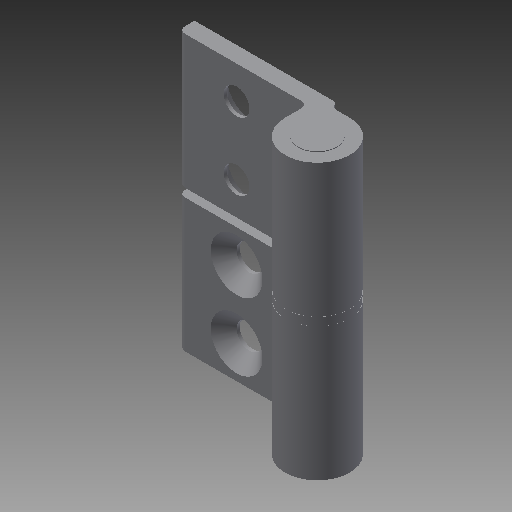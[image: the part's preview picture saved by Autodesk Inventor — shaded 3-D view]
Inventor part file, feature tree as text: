
AUTODESK INVENTOR PART (.ipt)
format: ipt  version: 2018 (Build 220112000, 112)  size: 186,880 bytes
history: native  units: mm
features: other x42, sketch x8, extrude x4, hole x4
ambient origin geometry x8: Origin, YZ Plane, XZ Plane, XY Plane, X Axis, Y Axis, Z Axis, Center Point
bodies: Solid1 (feature_tree)
feature tree (58):
  extrude  "Extrusion1"  Depth=85.5mm TaperAngle=0.0deg
  extrude  "Extrusion2"  Depth=41.25mm TaperAngle=0.0deg
  extrude  "Extrusion3"  [1 undecoded]
  extrude  "Extrusion4"  [1 undecoded]
  hole  "Drilling 1"  [1 undecoded]
  hole  "Drilling 2"  [1 undecoded]
  hole  "Drilling 3"  [1 undecoded]
  hole  "Drilling 4"  [1 undecoded]
  other  "side_2a_XY"
  other  "side_2a_YZ"
  other  "side_2a_ZX"
  other  "side_2a_X"
  other  "side_2a_Y"
  other  "side_2a_Z"
  other  "side_2a_Center"
  other  "side_2b_XY"
  other  "side_2b_YZ"
  other  "side_2b_ZX"
  other  "side_2b_X"
  other  "side_2b_Y"
  other  "side_2b_Z"
  other  "side_2b_Center"
  other  "side_1b_XY"
  other  "side_1b_YZ"
  other  "side_1b_ZX"
  other  "side_1b_X"
  other  "side_1b_Y"
  other  "side_1b_Z"
  other  "side_1b_Center"
  other  "side_3b_XY"
  other  "side_3b_YZ"
  other  "side_3b_ZX"
  other  "side_3b_X"
  other  "side_3b_Y"
  other  "side_3b_Z"
  other  "side_3b_Center"
  other  "side_1a_XY"
  other  "side_1a_YZ"
  other  "side_1a_ZX"
  other  "side_1a_X"
  other  "side_1a_Y"
  other  "side_1a_Z"
  other  "side_1a_Center"
  other  "side_3a_XY"
  other  "side_3a_YZ"
  other  "side_3a_ZX"
  other  "side_3a_X"
  other  "side_3a_Y"
  other  "side_3a_Z"
  other  "side_3a_Center"
  sketch  "Skizze_34"  dims[d22=8.0mm d23=6.0mm d24=16.0mm d25=2.0mm d26=15.707963mm d27=5.0mm d28=0.0mm]
  sketch  "Skizze_35"  dims[d29=8.0mm d30=6.0mm d31=16.0mm d32=2.0mm d33=15.707963mm d34=5.0mm d35=0.0mm]
  sketch  "Skizze_36"
  sketch  "Skizze_37"
  sketch  "Sketch5"  dims[d0=2.5mm d1=0.0mm d2=85.5mm d3=0.0mm]
  sketch  "Sketch6"  dims[d4=41.25mm d5=0.0mm d6=41.25mm d7=0.0mm]
  sketch  "Sketch7"  dims[d8=8.0mm d9=6.0mm d10=16.0mm d11=2.0mm d12=15.707963mm d13=5.0mm d14=0.0mm]
  sketch  "Sketch8"  dims[d15=8.0mm d16=6.0mm d17=16.0mm d18=2.0mm d19=15.707963mm d20=5.0mm d21=0.0mm]
note: 6 required parameter values undecoded (feature->parameter linkage not recoverable at this tier; creation-order binding heuristic only, values carry confidence <= 0.55)
